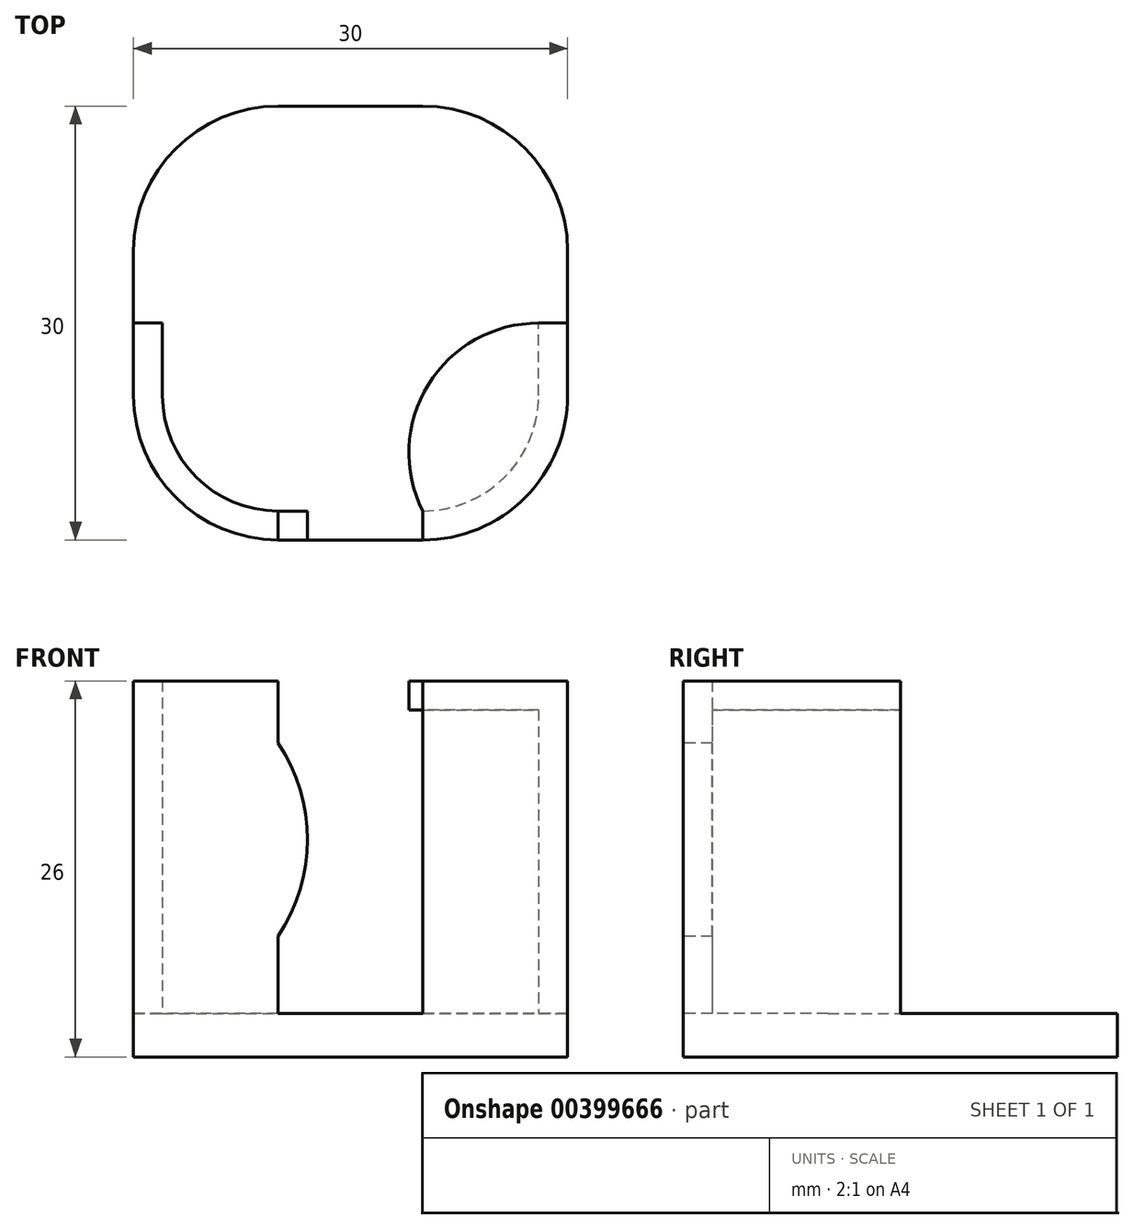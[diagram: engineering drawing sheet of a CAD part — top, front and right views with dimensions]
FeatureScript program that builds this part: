
annotation { "Feature Type Name" : "Feature", "Feature Type Description" : "" }
export const myFeature = defineFeature(function(context is Context, id is Id, definition is map)
    precondition{}
    {
        {
            var Q0;
            Q0=qCreatedBy(makeId("Top.planeOp"),FACE);
            var sketch = newSketch(context, id + "F0", { "sketchPlane" : qUnion([Q0])});
            skLineSegment(sketch, "E0.bottom", {"start": v(10, 0) * mm, "end": v(20, 0) * mm});
            skLineSegment(sketch, "E0.top", {"start": v(10, 30) * mm, "end": v(20, 30) * mm});
            skLineSegment(sketch, "E0.left", {"start": v(0, 10) * mm, "end": v(0, 20) * mm});
            skLineSegment(sketch, "E0.right", {"start": v(30, 10) * mm, "end": v(30, 20) * mm});
            skPoint(sketch, "E1.visualSharp", {"position": v(0, 30) * mm});
            skArc(sketch, "E1.filletArc", {"start": v(10, 30) * mm, "mid": v(2.93, 27.07) * mm, "end": v(0, 20) * mm});
            skPoint(sketch, "E2.visualSharp", {"position": v(30, 30) * mm});
            skArc(sketch, "E2.filletArc", {"start": v(30, 20) * mm, "mid": v(27.07, 27.07) * mm, "end": v(20, 30) * mm});
            skPoint(sketch, "E3.visualSharp", {"position": v(0, 0) * mm});
            skArc(sketch, "E3.filletArc", {"start": v(0, 10) * mm, "mid": v(2.93, 2.93) * mm, "end": v(10, 0) * mm});
            skPoint(sketch, "E4.visualSharp", {"position": v(30, 0) * mm});
            skArc(sketch, "E4.filletArc", {"start": v(20, 0) * mm, "mid": v(27.07, 2.93) * mm, "end": v(30, 10) * mm});
            skSolve(sketch);
        }
        {
            var Q0;
            Q0=makeQuery(id+"F0.imprint","IMPRINT",FACE,{"disambiguationData":[TD([[makeQuery(id+"F0.imprint","IMPRINT",EDGE,{"derivedFrom":sQuery(id+"F0.wireOp",EDGE,"E0.bottom")}),1.0]])]});
            extrude(context, id + "F1", {"entities" : qUnion([Q0]), "depth" : 3 * mm});
        }
        {
            var Q0;
            Q0=makeQuery(id+"F1.opExtrude","CAP_FACE",FACE,{"disambiguationData":[OSD([sQuery(id+"F0.wireOp",EDGE,"E0.bottom"),sQuery(id+"F0.wireOp",EDGE,"E0.top"),sQuery(id+"F0.wireOp",EDGE,"E0.left"),sQuery(id+"F0.wireOp",EDGE,"E0.right"),sQuery(id+"F0.wireOp",EDGE,"E1.filletArc"),sQuery(id+"F0.wireOp",EDGE,"E2.filletArc"),sQuery(id+"F0.wireOp",EDGE,"E3.filletArc"),sQuery(id+"F0.wireOp",EDGE,"E4.filletArc")])],"isStart":false});
            var sketch = newSketch(context, id + "F2", { "sketchPlane" : qUnion([Q0])});
            skLineSegment(sketch, "E5", {"start": v(0, 15) * mm, "end": v(0, 10) * mm});
            skLineSegment(sketch, "E6", {"start": v(30, 10) * mm, "end": v(30, 15) * mm});
            skArc(sketch, "E7.filletArc", {"start": v(0, 10) * mm, "mid": v(2.93, 2.93) * mm, "end": v(10, 0) * mm});
            skArc(sketch, "E8.filletArc", {"start": v(20, 0) * mm, "mid": v(27.07, 2.93) * mm, "end": v(30, 10) * mm});
            skArc(sketch, "E9.0", {"start": v(2, 10) * mm, "mid": v(4.34, 4.34) * mm, "end": v(10, 2) * mm});
            skLineSegment(sketch, "E9.1", {"start": v(2, 15) * mm, "end": v(2, 10) * mm});
            skLineSegment(sketch, "E10.0", {"start": v(28, 10) * mm, "end": v(28, 15) * mm});
            skArc(sketch, "E10.1", {"start": v(20, 2) * mm, "mid": v(25.66, 4.34) * mm, "end": v(28, 10) * mm});
            skLineSegment(sketch, "E11", {"start": v(0, 15) * mm, "end": v(2, 15) * mm});
            skLineSegment(sketch, "E12", {"start": v(10, 2) * mm, "end": v(10, 0) * mm});
            skLineSegment(sketch, "E13", {"start": v(20, 2) * mm, "end": v(20, 0) * mm});
            skLineSegment(sketch, "E14", {"start": v(28, 15) * mm, "end": v(30, 15) * mm});
            skSolve(sketch);
        }
        {
            var Q0;
            Q0=makeQuery(id+"F2.imprint","IMPRINT",FACE,{"disambiguationData":[TD([[makeQuery(id+"F2.imprint","IMPRINT",EDGE,{"derivedFrom":sQuery(id+"F2.wireOp",EDGE,"E5")}),-1.0]])]});
            var Q1;
            Q1=makeQuery(id+"F2.imprint","IMPRINT",FACE,{"disambiguationData":[TD([[makeQuery(id+"F2.imprint","IMPRINT",EDGE,{"derivedFrom":sQuery(id+"F2.wireOp",EDGE,"E6")}),1.0]])]});
            extrude(context, id + "F3", {"entities" : qUnion([Q0, Q1]), "operationType" : NewBodyOperationType.ADD, "depth" : 21 * mm});
        }
        {
            var Q0;
            Q0=makeQuery(id+"F3.opExtrude","CAP_FACE",FACE,{"disambiguationData":[OSD([sQuery(id+"F2.wireOp",EDGE,"E5"),sQuery(id+"F2.wireOp",EDGE,"E7.filletArc"),sQuery(id+"F2.wireOp",EDGE,"E9.0"),sQuery(id+"F2.wireOp",EDGE,"E9.1"),sQuery(id+"F2.wireOp",EDGE,"E11"),sQuery(id+"F2.wireOp",EDGE,"E12")])],"isStart":false});
            var sketch = newSketch(context, id + "F4", { "sketchPlane" : qUnion([Q0])});
            skLineSegment(sketch, "E15", {"start": v(0, 15) * mm, "end": v(0, 10) * mm});
            skLineSegment(sketch, "E16", {"start": v(30, 10) * mm, "end": v(30, 15) * mm});
            skPoint(sketch, "E17.visualSharp", {"position": v(0, 0) * mm});
            skArc(sketch, "E17.filletArc", {"start": v(0, 10) * mm, "mid": v(2.93, 2.93) * mm, "end": v(10, 0) * mm});
            skPoint(sketch, "E18.visualSharp", {"position": v(30, 0) * mm});
            skArc(sketch, "E18.filletArc", {"start": v(20, 0) * mm, "mid": v(27.07, 2.93) * mm, "end": v(30, 10) * mm});
            skLineSegment(sketch, "E19", {"start": v(10, 0) * mm, "end": v(10, 2) * mm});
            skLineSegment(sketch, "E20", {"start": v(2, 15) * mm, "end": v(0, 15) * mm});
            skLineSegment(sketch, "E21", {"start": v(20, 0) * mm, "end": v(20, 2) * mm});
            skLineSegment(sketch, "E22", {"start": v(28, 15) * mm, "end": v(30, 15) * mm});
            skArc(sketch, "E23", {"start": v(2, 15) * mm, "mid": v(9.63, 10.74) * mm, "end": v(10, 2) * mm});
            skArc(sketch, "E24", {"start": v(28, 15) * mm, "mid": v(20.37, 10.74) * mm, "end": v(20, 2) * mm});
            skSolve(sketch);
        }
        {
            var Q0;
            Q0=makeQuery(id+"F4.imprint","IMPRINT",FACE,{"disambiguationData":[TD([[makeQuery(id+"F4.imprint","IMPRINT",EDGE,{"derivedFrom":sQuery(id+"F4.wireOp",EDGE,"E15")}),-1.0]])]});
            var Q1;
            Q1=makeQuery(id+"F4.imprint","IMPRINT",FACE,{"disambiguationData":[TD([[makeQuery(id+"F4.imprint","IMPRINT",EDGE,{"derivedFrom":sQuery(id+"F4.wireOp",EDGE,"DHkWA1v5-H535-Fc1G-Q2Yv-l5H4Wd7Q0ZUm")}),1.0]])]});
            var Q2;
            Q2=makeQuery(id+"F4.imprint","IMPRINT",FACE,{"disambiguationData":[TD([[makeQuery(id+"F4.imprint","IMPRINT",EDGE,{"derivedFrom":sQuery(id+"F4.wireOp",EDGE,"E16")}),1.0]])]});
            var Q3;
            Q3=makeQuery(id+"F4.imprint","IMPRINT",FACE,{"disambiguationData":[TD([[makeQuery(id+"F4.imprint","IMPRINT",EDGE,{"derivedFrom":sQuery(id+"F4.wireOp",EDGE,"E23")}),-1.0]])]});
            extrude(context, id + "F5", {"entities" : qUnion([Q0, Q1, Q2, Q3]), "operationType" : NewBodyOperationType.ADD, "depth" : 2 * mm});
        }
        {
            var Q0;
            Q0=makeQuery(id+"F1.opExtrude","SWEPT_FACE",FACE,{"disambiguationData":[OSD([sQuery(id+"F0.wireOp",EDGE,"E0.bottom")])]});
            var sketch = newSketch(context, id + "F6", { "sketchPlane" : qUnion([Q0])});
            skLineSegment(sketch, "E25", {"start": v(-12.17, 15) * mm, "end": v(42.77, 15) * mm, "construction": true});
            skLineSegment(sketch, "E26", {"start": v(15, 30.77) * mm, "end": v(15, -12.25) * mm, "construction": true});
            skLineSegment(sketch, "E27", {"start": v(0, 0) * mm, "end": v(0, 26.08) * mm, "construction": true});
            skLineSegment(sketch, "E28.MirrorCS", {"start": v(30, 0) * mm, "end": v(30, 26.08) * mm, "construction": true});
            skPoint(sketch, "E29", {"position": v(0.03, 15.03) * mm});
            skArc(sketch, "E30", {"start": v(10, 8.35) * mm, "mid": v(12.03, 15.03) * mm, "end": v(10, 21.7) * mm});
            skLineSegment(sketch, "E31", {"start": v(10, 8.35) * mm, "end": v(10, 21.7) * mm});
            skArc(sketch, "E32.MirrorCS", {"start": v(20, 8.35) * mm, "mid": v(17.97, 15.03) * mm, "end": v(20, 21.7) * mm});
            skLineSegment(sketch, "E33.MirrorCS", {"start": v(20, 8.35) * mm, "end": v(20, 21.7) * mm});
            skSolve(sketch);
        }
        {
            var Q0;
            Q0=makeQuery(id+"F6.imprint","IMPRINT",FACE,{"disambiguationData":[TD([[makeQuery(id+"F6.imprint","IMPRINT",EDGE,{"derivedFrom":sQuery(id+"F6.wireOp",EDGE,"E30")}),1.0]])]});
            var Q1;
            Q1=makeQuery(id+"F6.imprint","IMPRINT",FACE,{"disambiguationData":[TD([[makeQuery(id+"F6.imprint","IMPRINT",EDGE,{"derivedFrom":sQuery(id+"F6.wireOp",EDGE,"E32.MirrorCS")}),-1.0]])]});
            extrude(context, id + "F7", {"entities" : qUnion([Q0, Q1]), "operationType" : NewBodyOperationType.ADD, "oppositeDirection" : true, "depth" : 2 * mm});
        }
    });
